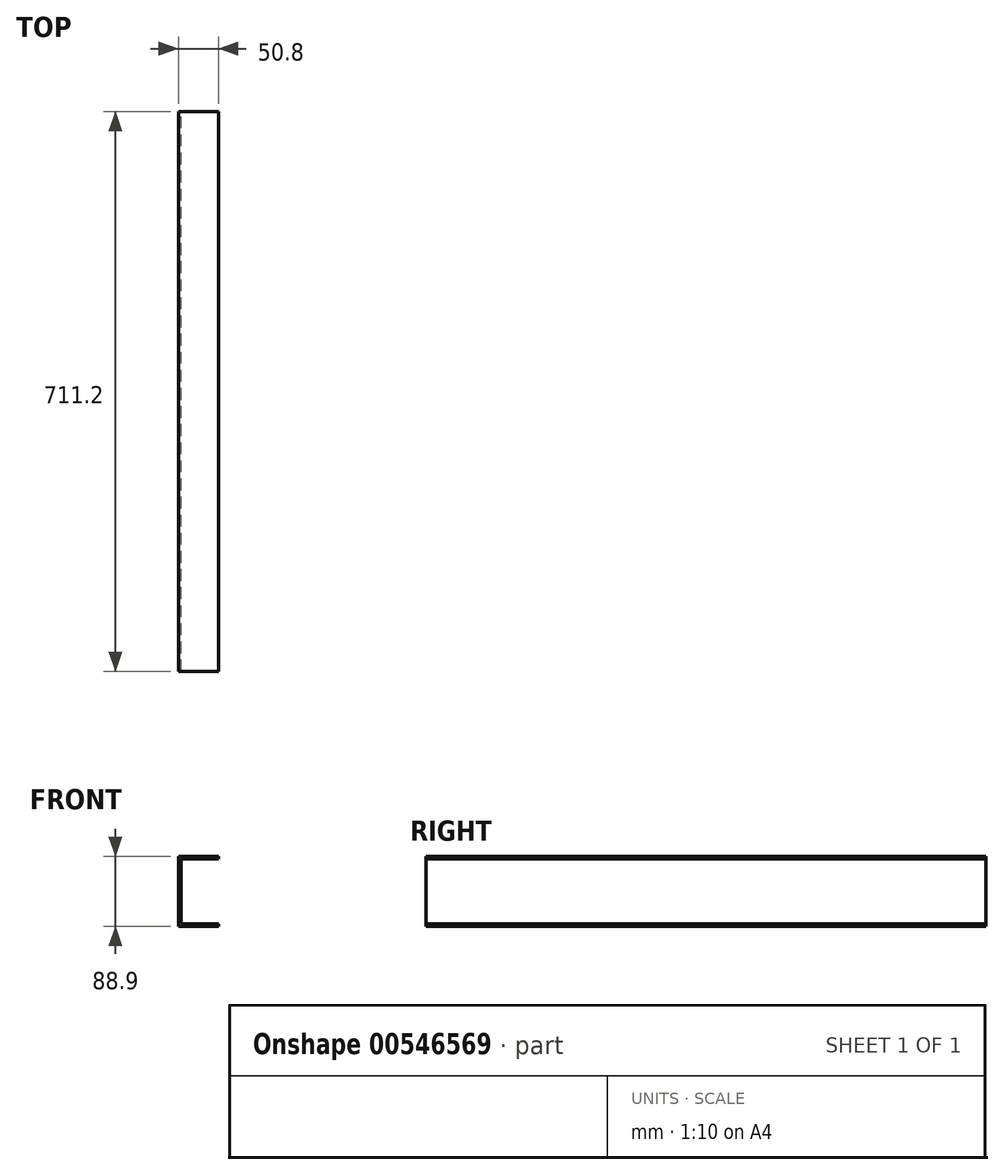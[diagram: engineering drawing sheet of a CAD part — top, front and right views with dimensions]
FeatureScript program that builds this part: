
annotation { "Feature Type Name" : "Feature", "Feature Type Description" : "" }
export const myFeature = defineFeature(function(context is Context, id is Id, definition is map)
    precondition{}
    {
        {
            var Q0;
            Q0=qCreatedBy(makeId("Front.planeOp"),FACE);
            var sketch = newSketch(context, id + "F0", { "sketchPlane" : qUnion([Q0])});
            skLineSegment(sketch, "E0.bottom", {"start": v(25.4, 44.45) * mm, "end": v(-25.4, 44.45) * mm});
            skLineSegment(sketch, "E0.top", {"start": v(25.4, -44.45) * mm, "end": v(-25.4, -44.45) * mm});
            skLineSegment(sketch, "E0.left", {"start": v(25.4, 44.45) * mm, "end": v(25.4, -44.45) * mm});
            skLineSegment(sketch, "E0.right", {"start": v(-25.4, 44.45) * mm, "end": v(-25.4, -44.45) * mm});
            skPoint(sketch, "E0.middle", {"position": v(0, 0) * mm});
            skSolve(sketch);
        }
        {
            var Q0;
            Q0=makeQuery(id+"F0.imprint","IMPRINT",FACE,{"disambiguationData":[TD([[makeQuery(id+"F0.imprint","IMPRINT",EDGE,{"derivedFrom":sQuery(id+"F0.wireOp",EDGE,"E0.bottom")}),1.0]])]});
            extrude(context, id + "F1", {"entities" : qUnion([Q0]), "depth" : 711.2 * mm, "offsetDistance" : 25.4 * mm});
        }
        {
            var Q0;
            Q0=makeQuery(id+"F1.opExtrude","SWEPT_FACE",FACE,{"disambiguationData":[OSD([sQuery(id+"F0.wireOp",EDGE,"E0.left")])]});
            var Q1;
            Q1=makeQuery(id+"F1.opExtrude","CAP_FACE",FACE,{"disambiguationData":[OSD([sQuery(id+"F0.wireOp",EDGE,"E0.bottom"),sQuery(id+"F0.wireOp",EDGE,"E0.top"),sQuery(id+"F0.wireOp",EDGE,"E0.left"),sQuery(id+"F0.wireOp",EDGE,"E0.right")])],"isStart":false});
            var Q2;
            Q2=makeQuery(id+"F1.opExtrude","CAP_FACE",FACE,{"disambiguationData":[OSD([sQuery(id+"F0.wireOp",EDGE,"E0.bottom"),sQuery(id+"F0.wireOp",EDGE,"E0.top"),sQuery(id+"F0.wireOp",EDGE,"E0.left"),sQuery(id+"F0.wireOp",EDGE,"E0.right")])],"isStart":true});
            shell(context, id + "F2", {"entities" : qUnion([Q0, Q1, Q2]), "thickness" : 3.17 * mm});
        }
    });
